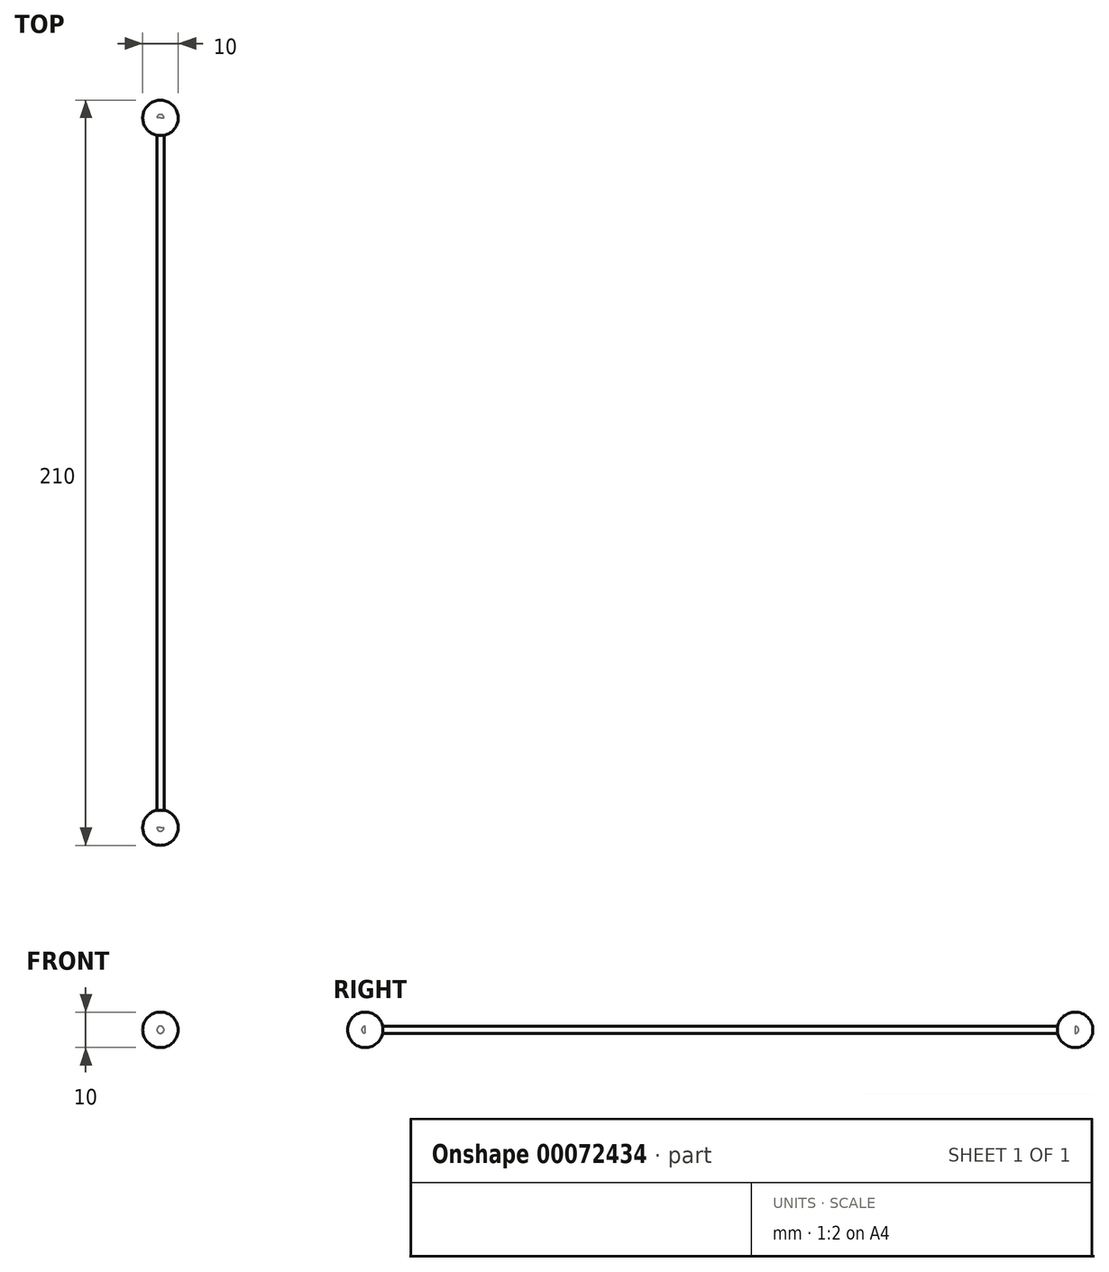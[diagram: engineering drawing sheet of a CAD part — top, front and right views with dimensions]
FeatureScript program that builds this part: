
annotation { "Feature Type Name" : "Feature", "Feature Type Description" : "" }
export const myFeature = defineFeature(function(context is Context, id is Id, definition is map)
    precondition{}
    {
        {
            var Q0;
            Q0=qCreatedBy(makeId("Front.planeOp"),FACE);
            var sketch = newSketch(context, id + "F0", { "sketchPlane" : qUnion([Q0])});
            skCircle(sketch, "E0", {"center": v(0, 0) * mm, "radius": 1 * mm});
            skSolve(sketch);
        }
        {
            var Q0;
            Q0 = qSketchRegion(id + "F0", true);
            extrude(context, id + "F1", {"entities" : qUnion([Q0]), "depth" : 100 * mm});
        }
        {
            var Q0;
            Q0=makeQuery(id+"F1.opExtrude","CAP_FACE",FACE,{"disambiguationData":[OSD([sQuery(id+"F0.wireOp",EDGE,"E0")])],"isStart":false});
            var sketch = newSketch(context, id + "F2", { "sketchPlane" : qUnion([Q0])});
            skCircle(sketch, "E1", {"center": v(0, 0) * mm, "radius": 5 * mm});
            skLineSegment(sketch, "E2", {"start": v(0, 5) * mm, "end": v(0, -5) * mm});
            skSolve(sketch);
        }
        {
            var Q0;
            {var subQ0=sQuery(id+"F2.wireOp",EDGE,"E2");var subQ1=sQuery(id+"F2.wireOp",EDGE,"E1");var subQ2=makeQuery(id+"F2.imprint","INTERSECT",VERTEX,{"disambiguationData":[OD(0.0)],"derivedFrom":[subQ1,subQ0]});Q0=makeQuery(id+"F2.imprint","IMPRINT",FACE,{"disambiguationData":[TD([[makeQuery(id+"F2.imprint","IMPRINT",EDGE,{"disambiguationData":[TD([[subQ2,-1.0]])],"derivedFrom":subQ1}),1.0]])]});}
            var Q1;
            Q1=sQuery(id+"F2.wireOp",EDGE,"E2");
            revolve(context, id + "F3", {"operationType" : NewBodyOperationType.ADD, "entities" : qUnion([Q0]), "axis" : qUnion([Q1]), "revolveType" : RevolveType.FULL});
        }
        {
            var Q0;
            Q0=makeQuery(id+"F1.opExtrude","SWEPT_BODY",BODY,{"disambiguationData":[OSD([sQuery(id+"F0.wireOp",EDGE,"E0")])]});
            var Q1;
            Q1=qCreatedBy(makeId("Front.planeOp"),FACE);
            mirror(context, id + "F4", {"operationType" : NewBodyOperationType.ADD, "entities" : qUnion([Q0]), "mirrorPlane" : qUnion([Q1])});
        }
    });
